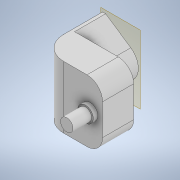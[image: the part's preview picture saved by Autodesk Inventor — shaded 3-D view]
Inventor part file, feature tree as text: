
AUTODESK INVENTOR PART (.ipt)
format: ipt  version: 2021 (Build 250183000, 183)  size: 147,968 bytes
history: native  units: mm
features: extrude x4, sketch x4, other x4, reference x3, plane x2, fillet x2, projected_geometry x1
ambient origin geometry x8: Origin, YZ Plane, XZ Plane, XY Plane, X Axis, Y Axis, Z Axis, Center Point
bodies: Solid1 (feature_tree)
feature tree (20):
  plane  "Work Plane1"
  extrude  "Extrusion1"  Depth=40.0mm
  sketch  "Sketch3"  dims[d3=40.0mm d4=20.0mm d5=0.0mm d6=15.0mm d7=10.0mm]
  plane  "Work Plane2"
  extrude  "Extrusion2"  Depth=20.0mm TaperAngle=0.0deg
  fillet  "Fillet1"  Radius=15.0mm
  fillet  "Fillet2"  Radius=10.0mm
  extrude  "Extrusion3"  Depth=10.0mm
  extrude  "Extrusion4"  Depth=3.0mm
  sketch  "Sketch2"  dims[d0=20.0mm d1=0.0mm d2=40.0mm]
  reference  "Reference2"
  reference  "Reference3"
  projected_geometry  "Projected Loop1"
  sketch  "Sketch4"  dims[d8=15.0mm d9=0.0mm d10=10.0mm]
  reference  "Reference4"
  sketch  "Sketch5"  dims[d11=3.0mm d12=0.0mm d13=0.5mm d14=0.872665mm]
  parser-record x1  (decoder bookkeeping rows leaked as tree rows — omitted from the tree; the rows remain in map.json)
  other  "ilmbt_3d_v1.iam"
  other  "knucle_MIR1:1"
  other  "base_:1"
note: 1 file-system path scrubbed to <path> (originals preserved in map.json)
